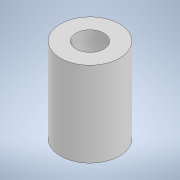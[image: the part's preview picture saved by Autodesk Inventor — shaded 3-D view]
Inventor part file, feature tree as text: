
AUTODESK INVENTOR PART (.ipt)
format: ipt  version: 2022 (Build 260153000, 153)  size: 94,208 bytes
history: native  units: in
note: dims shown in document units (in); Inventor stores cm internally (conversion verified against a paired STEP export)
features: extrude x1, sketch x1
ambient origin geometry x8: Origin, YZ Plane, XZ Plane, XY Plane, X Axis, Y Axis, Z Axis, Center Point
bodies: Solid1 (feature_tree)
feature tree (2):
  extrude  "Extrusion1"  Depth=0.5369in
  sketch  "Sketch1"  dims[d0=0.1757in d2=0.375in d3=0.5369in d4=0.0in]
